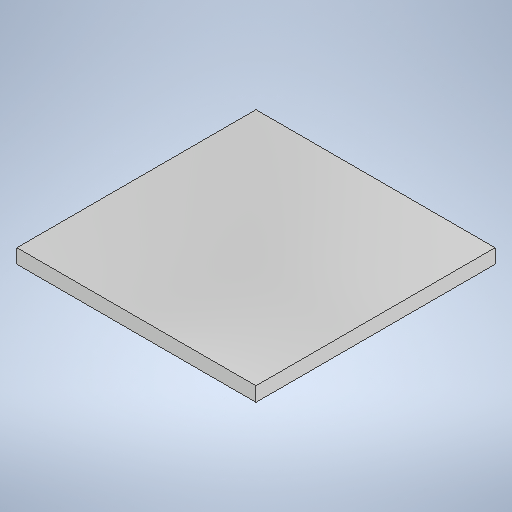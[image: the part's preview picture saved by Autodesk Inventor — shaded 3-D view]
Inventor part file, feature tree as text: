
AUTODESK INVENTOR PART (.ipt)
format: ipt  version: 2025.2 (Build 292293000, 293)  size: 203,776 bytes
history: native  units: mm
features: extrude x1, sketch x1
ambient origin geometry x8: Origin, YZ Plane, XZ Plane, XY Plane, X Axis, Y Axis, Z Axis, Center Point
bodies: Solid1 (feature_tree)
feature tree (2):
  extrude  "Extrusion1"  Depth=50.0mm
  sketch  "Sketch1"  dims[d0=50.0mm d1=50.0mm d2=3.0mm d3=0.0mm]
